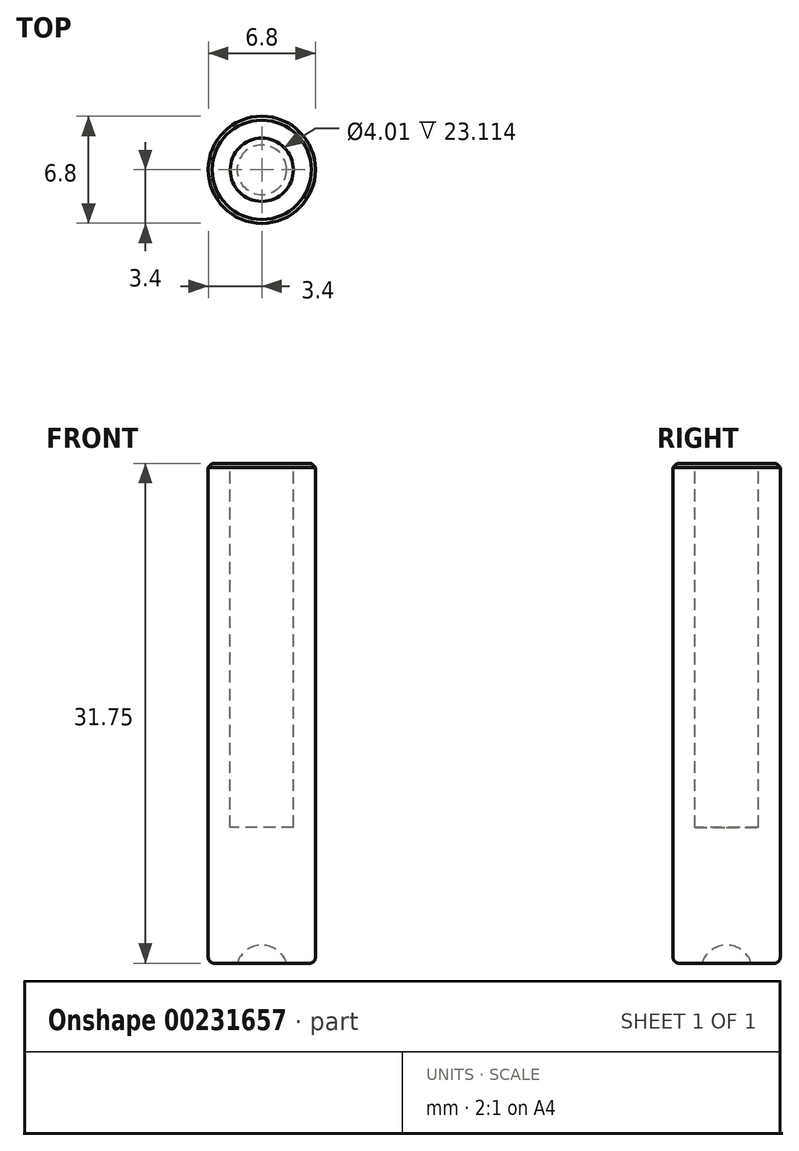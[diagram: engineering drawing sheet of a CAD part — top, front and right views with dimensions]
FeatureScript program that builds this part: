
annotation { "Feature Type Name" : "Feature", "Feature Type Description" : "" }
export const myFeature = defineFeature(function(context is Context, id is Id, definition is map)
    precondition{}
    {
        {
            var Q0;
            Q0=qCreatedBy(makeId("Top.planeOp"),FACE);
            var sketch = newSketch(context, id + "F0", { "sketchPlane" : qUnion([Q0])});
            skCircle(sketch, "E0", {"center": v(0, 0) * mm, "radius": 3.4 * mm});
            skSolve(sketch);
        }
        {
            var Q0;
            Q0 = qSketchRegion(id + "F0", true);
            extrude(context, id + "F1", {"entities" : qUnion([Q0]), "depth" : 31.75 * mm});
        }
        {
            var Q0;
            Q0=makeQuery(id+"F1.opExtrude","CAP_FACE",FACE,{"disambiguationData":[OSD([sQuery(id+"F0.wireOp",EDGE,"E0")])],"isStart":false});
            var sketch = newSketch(context, id + "F2", { "sketchPlane" : qUnion([Q0])});
            skCircle(sketch, "E1", {"center": v(0, 0) * mm, "radius": 2 * mm});
            skSolve(sketch);
        }
        {
            var Q0;
            Q0 = qSketchRegion(id + "F2", true);
            extrude(context, id + "F3", {"entities" : qUnion([Q0]), "operationType" : NewBodyOperationType.REMOVE, "oppositeDirection" : true, "depth" : 23.1 * mm});
        }
        {
            var Q0;
            Q0=makeQuery(id+"F1.opExtrude","CAP_FACE",FACE,{"disambiguationData":[OSD([sQuery(id+"F0.wireOp",EDGE,"E0")])],"isStart":true});
            cPlane(context, id + "F4", {"entities" : qUnion([Q0]), "cplaneType" : CPlaneType.OFFSET, "offset" : 0.5 * mm, "width" : 152.4 * mm, "height" : 152.4 * mm});
        }
        {
            var Q0;
            Q0=qCreatedBy(id+"F4.planeOp",FACE);
            var sketch = newSketch(context, id + "F5", { "sketchPlane" : qUnion([Q0])});
            skLineSegment(sketch, "E2", {"start": v(0, -4.75) * mm, "end": v(0, 5.04) * mm, "construction": true});
            skArc(sketch, "E3", {"start": v(0, -1.65) * mm, "mid": v(-1.65, 0) * mm, "end": v(0, 1.65) * mm});
            skLineSegment(sketch, "E4", {"start": v(0, 1.65) * mm, "end": v(0, -1.65) * mm});
            skSolve(sketch);
        }
        {
            var Q0;
            Q0 = qSketchRegion(id + "F5", true);
            var Q1;
            Q1=sQuery(id+"F5.wireOp",EDGE,"E2");
            revolve(context, id + "F6", {"operationType" : NewBodyOperationType.REMOVE, "entities" : qUnion([Q0]), "axis" : qUnion([Q1]), "revolveType" : RevolveType.FULL});
        }
        {
            var Q0;
            Q0=makeQuery(id+"F1.opExtrude","CAP_EDGE",EDGE,{"disambiguationData":[OSD([sQuery(id+"F0.wireOp",EDGE,"E0")])],"isStart":true});
            fillet(context, id + "F7", {"entities" : qUnion([Q0]), "radius" : 0.38 * mm, "tangentPropagation" : true, "allowEdgeOverflow" : false});
        }
        {
            var Q0;
            Q0=makeQuery(id+"F1.opExtrude","CAP_EDGE",EDGE,{"disambiguationData":[OSD([sQuery(id+"F0.wireOp",EDGE,"E0")])],"isStart":false});
            var Q1;
            Q1=makeQuery(id+"F3.boolean.opBoolean","COPY",EDGE,{"derivedFrom":makeQuery(id+"F3.opExtrude","CAP_EDGE",EDGE,{"disambiguationData":[OSD([sQuery(id+"F2.wireOp",EDGE,"E1")])],"isStart":true})});
            chamfer(context, id + "F8", {"entities" : qUnion([Q0, Q1]), "width" : 0.25 * mm, "tangentPropagation" : true});
        }
    });
